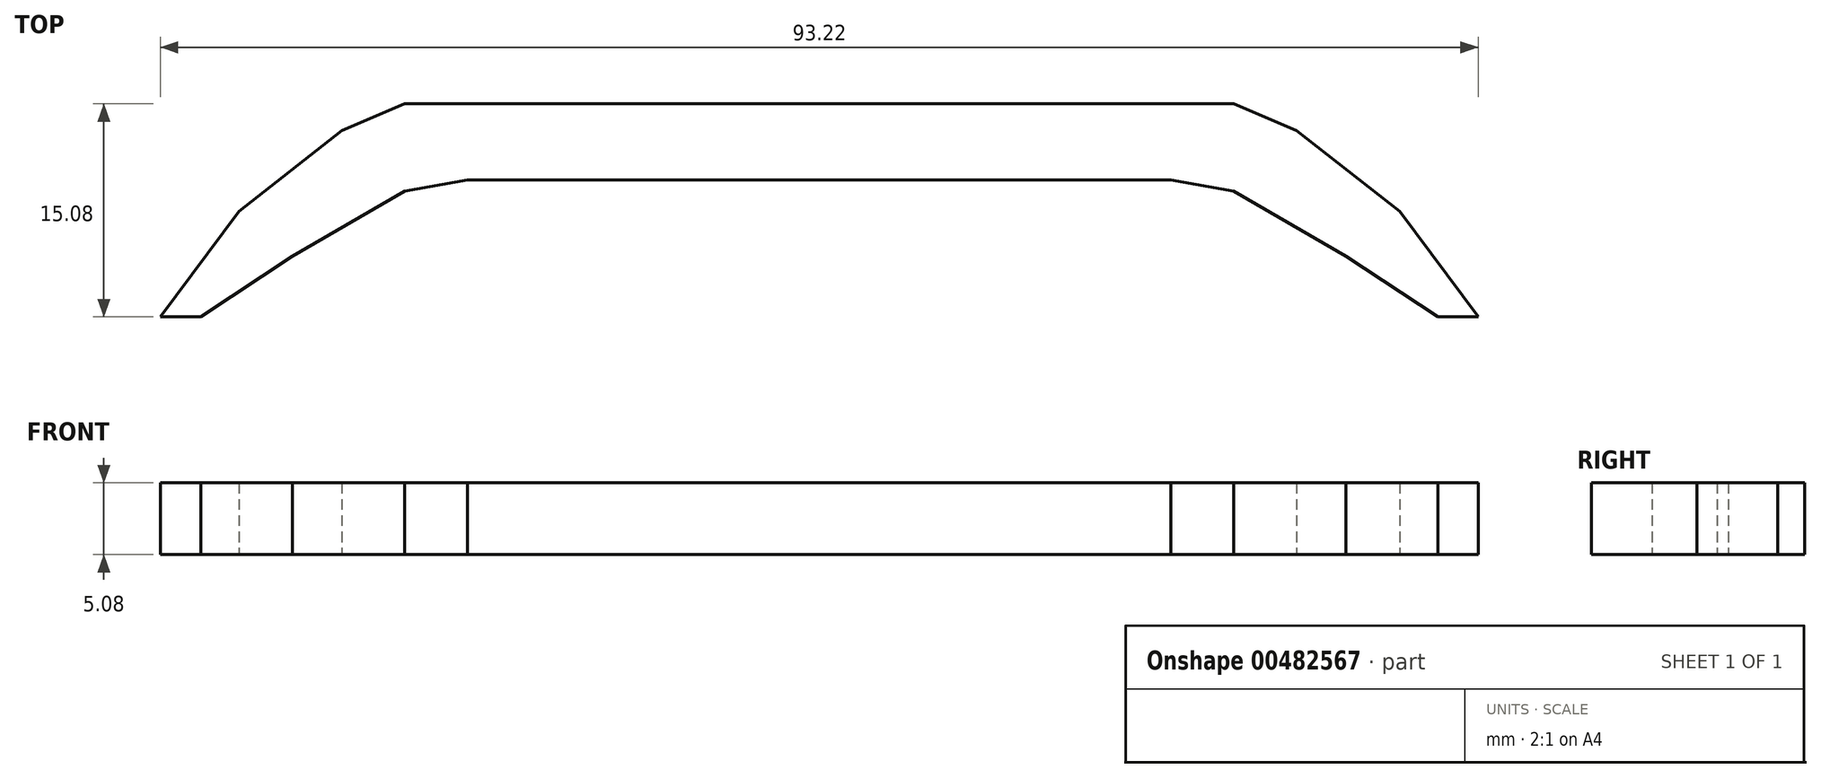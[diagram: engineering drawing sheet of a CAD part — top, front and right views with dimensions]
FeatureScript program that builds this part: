
annotation { "Feature Type Name" : "Feature", "Feature Type Description" : "" }
export const myFeature = defineFeature(function(context is Context, id is Id, definition is map)
    precondition{}
    {
        {
            var Q0;
            Q0=qCreatedBy(makeId("Top.planeOp"),FACE);
            var sketch = newSketch(context, id + "F0", { "sketchPlane" : qUnion([Q0])});
            skLineSegment(sketch, "E0.bottom", {"start": v(0, 28.54) * mm, "end": v(-24.87, 28.54) * mm});
            skLineSegment(sketch, "E0.top", {"start": v(0, 23.14) * mm, "end": v(-24.87, 23.14) * mm});
            skLineSegment(sketch, "E0.left", {"start": v(0, 28.54) * mm, "end": v(0, 23.14) * mm});
            skLineSegment(sketch, "E0.right", {"start": v(-24.87, 28.54) * mm, "end": v(-24.87, 23.14) * mm});
            skLineSegment(sketch, "E1", {"start": v(-24.87, 28.54) * mm, "end": v(-29.32, 28.54) * mm});
            skLineSegment(sketch, "E2", {"start": v(-29.32, 28.54) * mm, "end": v(-33.76, 26.63) * mm});
            skLineSegment(sketch, "E3", {"start": v(-33.76, 26.63) * mm, "end": v(-41.06, 20.92) * mm});
            skLineSegment(sketch, "E4", {"start": v(-41.06, 20.92) * mm, "end": v(-46.61, 13.46) * mm});
            skLineSegment(sketch, "E5", {"start": v(-46.61, 13.46) * mm, "end": v(-43.76, 13.46) * mm});
            skLineSegment(sketch, "E6", {"start": v(-43.76, 13.46) * mm, "end": v(-37.25, 17.75) * mm});
            skLineSegment(sketch, "E7", {"start": v(-37.25, 17.75) * mm, "end": v(-29.32, 22.35) * mm});
            skLineSegment(sketch, "E8", {"start": v(-29.32, 22.35) * mm, "end": v(-24.87, 23.14) * mm});
            skLineSegment(sketch, "E9.MirrorCS", {"start": v(46.61, 13.46) * mm, "end": v(43.76, 13.46) * mm});
            skLineSegment(sketch, "E10.MirrorCS", {"start": v(37.25, 17.75) * mm, "end": v(29.32, 22.35) * mm});
            skLineSegment(sketch, "E11.MirrorCS", {"start": v(29.32, 28.54) * mm, "end": v(33.76, 26.63) * mm});
            skLineSegment(sketch, "E12.MirrorCS", {"start": v(43.76, 13.46) * mm, "end": v(37.25, 17.75) * mm});
            skLineSegment(sketch, "E13.MirrorCS", {"start": v(24.87, 28.54) * mm, "end": v(29.32, 28.54) * mm});
            skLineSegment(sketch, "E14.MirrorCS", {"start": v(0, 23.14) * mm, "end": v(24.87, 23.14) * mm});
            skLineSegment(sketch, "E15.MirrorCS", {"start": v(24.87, 28.54) * mm, "end": v(24.87, 23.14) * mm});
            skLineSegment(sketch, "E16.MirrorCS", {"start": v(33.76, 26.63) * mm, "end": v(41.06, 20.92) * mm});
            skLineSegment(sketch, "E17.MirrorCS", {"start": v(41.06, 20.92) * mm, "end": v(46.61, 13.46) * mm});
            skLineSegment(sketch, "E18.MirrorCS", {"start": v(29.32, 22.35) * mm, "end": v(24.87, 23.14) * mm});
            skLineSegment(sketch, "E19.MirrorCS", {"start": v(0, 28.54) * mm, "end": v(24.87, 28.54) * mm});
            skSolve(sketch);
        }
        {
            var Q0;
            Q0 = qSketchRegion(id + "F0", true);
            extrude(context, id + "F1", {"entities" : qUnion([Q0]), "depth" : 5.08 * mm});
        }
    });
